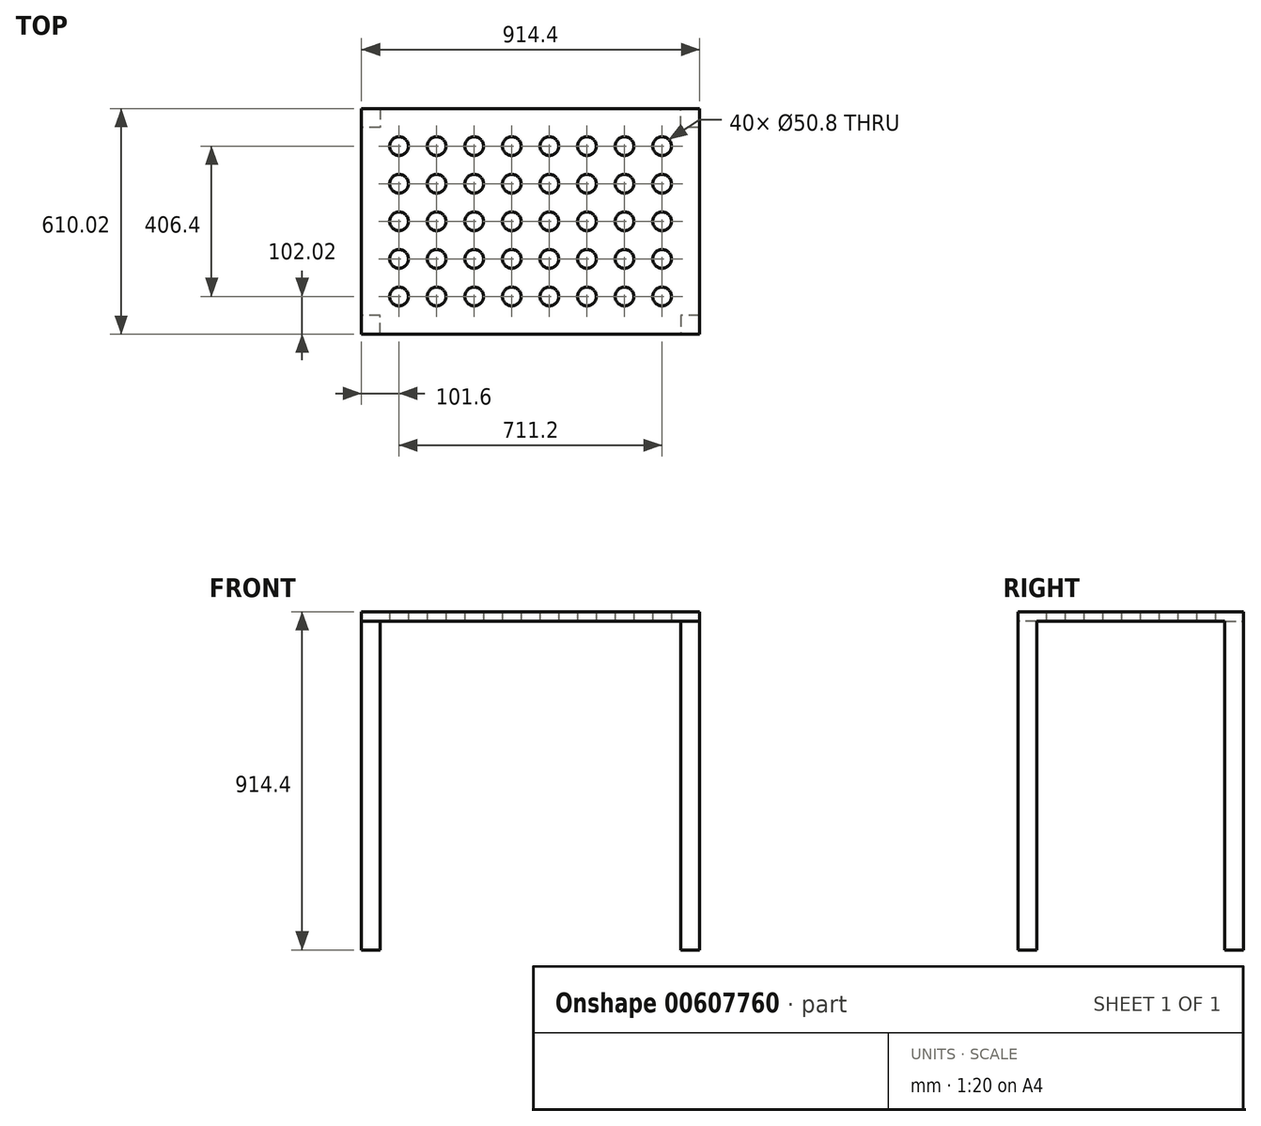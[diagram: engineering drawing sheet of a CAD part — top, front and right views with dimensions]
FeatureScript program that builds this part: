
annotation { "Feature Type Name" : "Feature", "Feature Type Description" : "" }
export const myFeature = defineFeature(function(context is Context, id is Id, definition is map)
    precondition{}
    {
        {
            var Q0;
            Q0=qCreatedBy(makeId("Top.planeOp"),FACE);
            var sketch = newSketch(context, id + "F0", { "sketchPlane" : qUnion([Q0])});
            skLineSegment(sketch, "E0", {"start": v(0, 0) * mm, "end": v(-914.4, 0) * mm});
            skLineSegment(sketch, "E1", {"start": v(-914.4, 0) * mm, "end": v(-914.4, -609.6) * mm});
            skLineSegment(sketch, "E2", {"start": v(-914.4, -609.6) * mm, "end": v(0, -609.6) * mm});
            skLineSegment(sketch, "E3", {"start": v(0, -609.6) * mm, "end": v(0, 0) * mm});
            skCircle(sketch, "E4", {"center": v(-812.8, -101.6) * mm, "radius": 25.4 * mm});
            skCircle(sketch, "E5", {"center": v(-711.2, -101.6) * mm, "radius": 25.4 * mm});
            skCircle(sketch, "E6", {"center": v(-609.6, -101.6) * mm, "radius": 25.4 * mm});
            skCircle(sketch, "E7", {"center": v(-508, -101.6) * mm, "radius": 25.4 * mm});
            skCircle(sketch, "E8", {"center": v(-406.4, -101.6) * mm, "radius": 25.4 * mm});
            skCircle(sketch, "E9", {"center": v(-304.8, -101.6) * mm, "radius": 25.4 * mm});
            skCircle(sketch, "E10", {"center": v(-203.2, -101.6) * mm, "radius": 25.4 * mm});
            skCircle(sketch, "E11", {"center": v(-101.6, -101.6) * mm, "radius": 25.4 * mm});
            skCircle(sketch, "E12", {"center": v(-812.8, -203.2) * mm, "radius": 25.4 * mm});
            skCircle(sketch, "E13", {"center": v(-711.2, -203.2) * mm, "radius": 25.4 * mm});
            skCircle(sketch, "E14", {"center": v(-609.6, -203.2) * mm, "radius": 25.4 * mm});
            skCircle(sketch, "E15", {"center": v(-508, -203.2) * mm, "radius": 25.4 * mm});
            skCircle(sketch, "E16", {"center": v(-406.4, -203.2) * mm, "radius": 25.4 * mm});
            skCircle(sketch, "E17", {"center": v(-304.8, -203.2) * mm, "radius": 25.4 * mm});
            skCircle(sketch, "E18", {"center": v(-203.2, -203.2) * mm, "radius": 25.4 * mm});
            skCircle(sketch, "E19", {"center": v(-101.6, -203.2) * mm, "radius": 25.4 * mm});
            skCircle(sketch, "E20", {"center": v(-812.8, -304.8) * mm, "radius": 25.4 * mm});
            skCircle(sketch, "E21", {"center": v(-711.2, -304.8) * mm, "radius": 25.4 * mm});
            skCircle(sketch, "E22", {"center": v(-609.6, -304.8) * mm, "radius": 25.4 * mm});
            skCircle(sketch, "E23", {"center": v(-508, -304.8) * mm, "radius": 25.4 * mm});
            skCircle(sketch, "E24", {"center": v(-406.4, -304.8) * mm, "radius": 25.4 * mm});
            skCircle(sketch, "E25", {"center": v(-304.8, -304.8) * mm, "radius": 25.4 * mm});
            skCircle(sketch, "E26", {"center": v(-203.2, -304.8) * mm, "radius": 25.4 * mm});
            skCircle(sketch, "E27", {"center": v(-101.6, -304.8) * mm, "radius": 25.4 * mm});
            skCircle(sketch, "E28", {"center": v(-812.8, -406.4) * mm, "radius": 25.4 * mm});
            skCircle(sketch, "E29", {"center": v(-711.2, -406.4) * mm, "radius": 25.4 * mm});
            skCircle(sketch, "E30", {"center": v(-609.6, -406.4) * mm, "radius": 25.4 * mm});
            skCircle(sketch, "E31", {"center": v(-508, -406.4) * mm, "radius": 25.4 * mm});
            skCircle(sketch, "E32", {"center": v(-406.4, -406.4) * mm, "radius": 25.4 * mm});
            skCircle(sketch, "E33", {"center": v(-304.8, -406.4) * mm, "radius": 25.4 * mm});
            skCircle(sketch, "E34", {"center": v(-203.2, -406.4) * mm, "radius": 25.4 * mm});
            skCircle(sketch, "E35", {"center": v(-101.6, -406.4) * mm, "radius": 25.4 * mm});
            skCircle(sketch, "E36", {"center": v(-812.8, -508) * mm, "radius": 25.4 * mm});
            skCircle(sketch, "E37", {"center": v(-711.2, -508) * mm, "radius": 25.4 * mm});
            skCircle(sketch, "E38", {"center": v(-609.6, -508) * mm, "radius": 25.4 * mm});
            skCircle(sketch, "E39", {"center": v(-508, -508) * mm, "radius": 25.4 * mm});
            skCircle(sketch, "E40", {"center": v(-406.4, -508) * mm, "radius": 25.4 * mm});
            skCircle(sketch, "E41", {"center": v(-304.8, -508) * mm, "radius": 25.4 * mm});
            skCircle(sketch, "E42", {"center": v(-203.2, -508) * mm, "radius": 25.4 * mm});
            skCircle(sketch, "E43", {"center": v(-101.6, -508) * mm, "radius": 25.4 * mm});
            skSolve(sketch);
        }
        {
            var Q0;
            Q0=makeQuery(id+"F0.imprint","IMPRINT",FACE,{"disambiguationData":[TD([[makeQuery(id+"F0.imprint","IMPRINT",EDGE,{"derivedFrom":sQuery(id+"F0.wireOp",EDGE,"E0")}),1.0]])]});
            extrude(context, id + "F1", {"entities" : qUnion([Q0]), "depth" : 25.4 * mm, "offsetDistance" : 25.4 * mm});
        }
        {
            var Q0;
            Q0=qCreatedBy(makeId("Top.planeOp"),FACE);
            var sketch = newSketch(context, id + "F2", { "sketchPlane" : qUnion([Q0])});
            skLineSegment(sketch, "E44", {"start": v(-914.28, 0) * mm, "end": v(-863.48, 0) * mm});
            skLineSegment(sketch, "E45", {"start": v(-863.48, 0) * mm, "end": v(-863.48, -50.8) * mm});
            skLineSegment(sketch, "E46", {"start": v(-863.48, -50.8) * mm, "end": v(-914.28, -50.8) * mm});
            skLineSegment(sketch, "E47", {"start": v(-914.28, -50.8) * mm, "end": v(-914.28, 0) * mm});
            skLineSegment(sketch, "E48", {"start": v(-914.28, -610.02) * mm, "end": v(-863.48, -610.02) * mm});
            skLineSegment(sketch, "E49", {"start": v(-863.48, -610.02) * mm, "end": v(-863.48, -559.22) * mm});
            skLineSegment(sketch, "E50", {"start": v(-863.48, -559.22) * mm, "end": v(-914.28, -559.22) * mm});
            skLineSegment(sketch, "E51", {"start": v(-914.28, -559.22) * mm, "end": v(-914.28, -610.02) * mm});
            skLineSegment(sketch, "E52", {"start": v(0, -610.02) * mm, "end": v(0, -559.22) * mm});
            skLineSegment(sketch, "E53", {"start": v(0, -559.22) * mm, "end": v(-50.8, -559.22) * mm});
            skLineSegment(sketch, "E54", {"start": v(-50.8, -559.22) * mm, "end": v(-50.8, -610.02) * mm});
            skLineSegment(sketch, "E55", {"start": v(-50.8, -610.02) * mm, "end": v(0, -610.02) * mm});
            skLineSegment(sketch, "E56", {"start": v(0, 0) * mm, "end": v(0, -50.8) * mm});
            skLineSegment(sketch, "E57", {"start": v(0, -50.8) * mm, "end": v(-50.8, -50.8) * mm});
            skLineSegment(sketch, "E58", {"start": v(-50.8, -50.8) * mm, "end": v(-50.8, 0) * mm});
            skLineSegment(sketch, "E59", {"start": v(-50.8, 0) * mm, "end": v(0, 0) * mm});
            skSolve(sketch);
        }
        {
            var Q0;
            Q0=makeQuery(id+"F2.imprint","IMPRINT",FACE,{"disambiguationData":[TD([[makeQuery(id+"F2.imprint","IMPRINT",EDGE,{"derivedFrom":sQuery(id+"F2.wireOp",EDGE,"E48")}),1.0]])]});
            var Q1;
            Q1=makeQuery(id+"F2.imprint","IMPRINT",FACE,{"disambiguationData":[TD([[makeQuery(id+"F2.imprint","IMPRINT",EDGE,{"derivedFrom":sQuery(id+"F2.wireOp",EDGE,"E52")}),1.0]])]});
            var Q2;
            Q2=makeQuery(id+"F2.imprint","IMPRINT",FACE,{"disambiguationData":[TD([[makeQuery(id+"F2.imprint","IMPRINT",EDGE,{"derivedFrom":sQuery(id+"F2.wireOp",EDGE,"E56")}),-1.0]])]});
            var Q3;
            Q3=makeQuery(id+"F2.imprint","IMPRINT",FACE,{"disambiguationData":[TD([[makeQuery(id+"F2.imprint","IMPRINT",EDGE,{"derivedFrom":sQuery(id+"F2.wireOp",EDGE,"E44")}),-1.0]])]});
            extrude(context, id + "F3", {"entities" : qUnion([Q0, Q1, Q2, Q3]), "operationType" : NewBodyOperationType.ADD, "depth" : -889 * mm, "offsetDistance" : 25.4 * mm});
        }
    });
